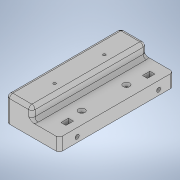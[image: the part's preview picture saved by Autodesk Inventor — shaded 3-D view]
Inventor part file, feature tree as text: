
AUTODESK INVENTOR PART (.ipt)
format: ipt  version: 2020 (Build 240168000, 168)  size: 281,600 bytes
history: native  units: in
note: dims shown in document units (in); Inventor stores cm internally (conversion verified against a paired STEP export)
features: extrude x7, sketch x7, other x6, reference x4, fillet x2, chamfer x1, projected_geometry x1
ambient origin geometry x8: Origin, YZ Plane, XZ Plane, XY Plane, X Axis, Y Axis, Z Axis, Center Point
bodies: Body1 (feature_tree)
feature tree (28):
  other  "Твердое тело1"
  extrude  "Выдавливание1"  Depth=0.1181in TaperAngle=0.0deg
  extrude  "Выдавливание2"  Depth=0.1181in TaperAngle=0.0deg
  sketch  "Эскиз3"
  other  "РабПлоскость1"
  extrude  "Выдавливание3"  Depth=0.1181in TaperAngle=0.0deg
  other  "Толщина1"
  fillet  "Сопряжение1"  Radius=0.1in
  extrude  "Выдавливание4"  Depth=0.1in
  fillet  "Сопряжение2"  Radius=0.125in
  chamfer  "Фаска1"  Distance=0.315in
  extrude  "Выдавливание5"  Depth=0.315in
  extrude  "Выдавливание6"  Depth=0.3937in TaperAngle=0.0deg
  extrude  "Выдавливание7"  Depth=0.125in
  sketch  "Эскиз2"
  reference  "Ссылка1"
  reference  "Ссылка2"
  reference  "Ссылка3"
  reference  "Ссылка4"
  sketch  "Эскиз4"
  sketch  "Эскиз5"
  projected_geometry  "Спроецированная петля1"
  sketch  "Эскиз6"
  sketch  "Эскиз7"
  sketch  "Эскиз1"
  other  "realsenses_plate_v2.ipt.iam"
  other  "Intel RealSense T265:1"
  other  "body:1"
